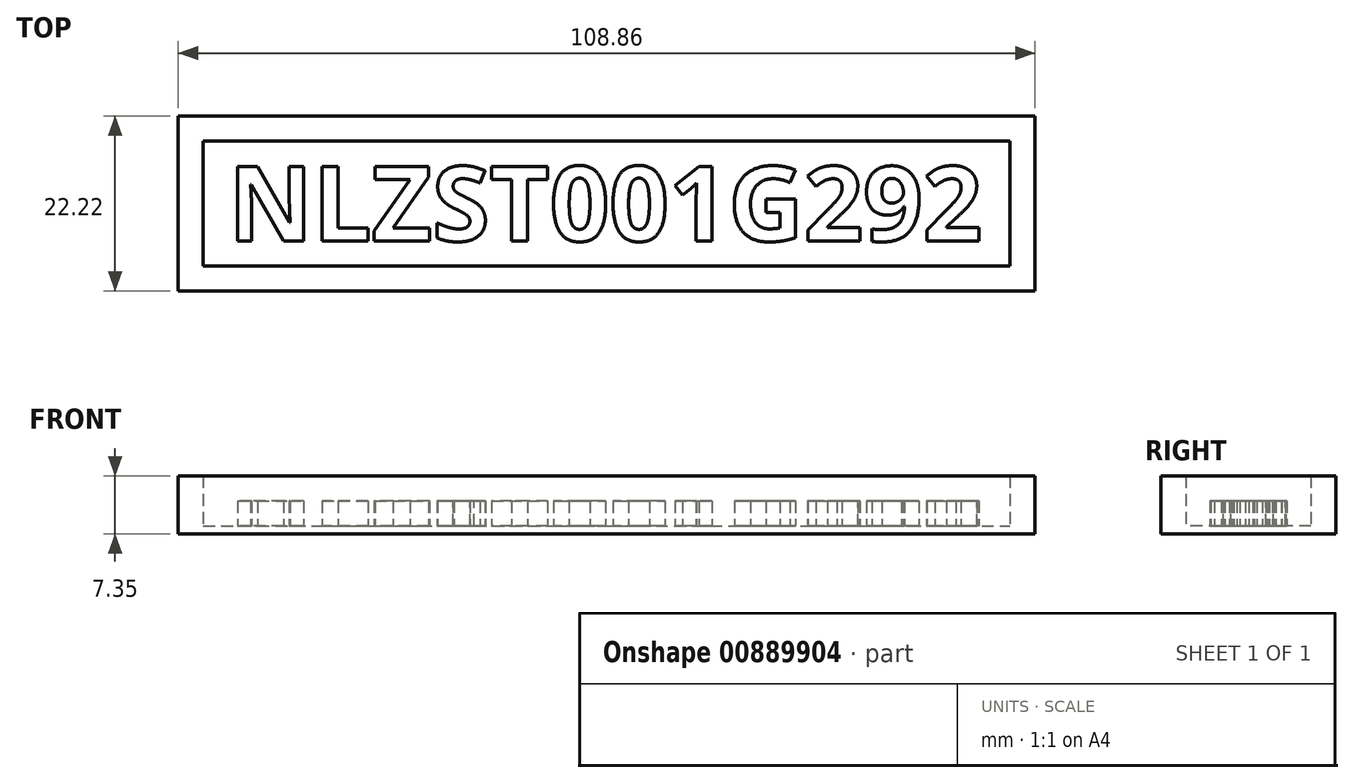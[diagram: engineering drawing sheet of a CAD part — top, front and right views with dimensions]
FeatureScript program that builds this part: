
annotation { "Feature Type Name" : "Feature", "Feature Type Description" : "" }
export const myFeature = defineFeature(function(context is Context, id is Id, definition is map)
    precondition{}
    {
        {
            var Q0;
            Q0=qCreatedBy(makeId("Top.planeOp"),FACE);
            var sketch = newSketch(context, id + "F0", { "sketchPlane" : qUnion([Q0])});
            skText(sketch, "E0", { "text": "NLZST001G292", "fontName": "OpenSans-Bold.ttf"});
            skLineSegment(sketch, "E1.bottom", {"start": v(-52.36, -1.8) * mm, "end": v(50.15, -1.8) * mm, "construction": true});
            skLineSegment(sketch, "E1.top", {"start": v(-52.36, 14.08) * mm, "end": v(50.15, 14.08) * mm, "construction": true});
            skLineSegment(sketch, "E1.left", {"start": v(-52.36, -1.8) * mm, "end": v(-52.36, 14.08) * mm, "construction": true});
            skLineSegment(sketch, "E1.right", {"start": v(50.15, -1.8) * mm, "end": v(50.15, 14.08) * mm, "construction": true});
            const initialGuessF0  = {"E0": [-0.04919, 0.00138, 1, 0, 0.00953]};
            skSetInitialGuess(sketch, initialGuessF0);
            skSolve(sketch);
        }
        {
            var Q0;
            Q0=qCreatedBy(makeId("Top.planeOp"),FACE);
            var sketch = newSketch(context, id + "F1", { "sketchPlane" : qUnion([Q0])});
            skLineSegment(sketch, "E2.bottom", {"start": v(-52.36, 14.08) * mm, "end": v(50.15, 14.08) * mm});
            skLineSegment(sketch, "E2.top", {"start": v(-52.36, -1.8) * mm, "end": v(50.15, -1.8) * mm});
            skLineSegment(sketch, "E2.left", {"start": v(-52.36, 14.08) * mm, "end": v(-52.36, -1.8) * mm});
            skLineSegment(sketch, "E2.right", {"start": v(50.15, 14.08) * mm, "end": v(50.15, -1.8) * mm});
            skSolve(sketch);
        }
        {
            var Q0;
            Q0 = qSketchRegion(id + "F1", true);
            extrude(context, id + "F2", {"entities" : qUnion([Q0]), "oppositeDirection" : true, "depth" : 1 * mm, "offsetDistance" : 25.4 * mm});
        }
        {
            var Q0;
            Q0 = qSketchRegion(id + "F0", true);
            extrude(context, id + "F3", {"entities" : qUnion([Q0]), "operationType" : NewBodyOperationType.ADD, "depth" : 3.17 * mm, "offsetDistance" : 25.4 * mm});
        }
        {
            var Q0;
            Q0=qCreatedBy(makeId("Top.planeOp"),FACE);
            var sketch = newSketch(context, id + "F4", { "sketchPlane" : qUnion([Q0])});
            skLineSegment(sketch, "E3.bottom", {"start": v(50.15, 14.08) * mm, "end": v(-52.36, 14.08) * mm});
            skLineSegment(sketch, "E3.top", {"start": v(50.15, -1.8) * mm, "end": v(-52.36, -1.8) * mm});
            skLineSegment(sketch, "E3.left", {"start": v(50.15, -1.8) * mm, "end": v(50.15, 14.08) * mm});
            skLineSegment(sketch, "E3.right", {"start": v(-52.36, -1.8) * mm, "end": v(-52.36, 14.08) * mm});
            skLineSegment(sketch, "E4", {"start": v(50.15, 6.14) * mm, "end": v(-1.1, 6.14) * mm, "construction": true});
            skLineSegment(sketch, "E5", {"start": v(-1.1, 6.14) * mm, "end": v(-1.1, 14.08) * mm, "construction": true});
            skLineSegment(sketch, "E6.bottom", {"start": v(-55.54, -4.97) * mm, "end": v(53.32, -4.97) * mm});
            skLineSegment(sketch, "E6.top", {"start": v(-55.54, 17.25) * mm, "end": v(53.32, 17.25) * mm});
            skLineSegment(sketch, "E6.left", {"start": v(-55.54, 17.25) * mm, "end": v(-55.54, -4.97) * mm});
            skLineSegment(sketch, "E6.right", {"start": v(53.32, 17.25) * mm, "end": v(53.32, -4.97) * mm});
            skPoint(sketch, "E6.middle", {"position": v(-1.1, 6.14) * mm});
            skSolve(sketch);
        }
        {
            var Q0;
            Q0 = qSketchRegion(id + "F4", true);
            var Q1;
            Q1=makeQuery(id+"F2.opExtrude","CAP_FACE",FACE,{"disambiguationData":[OSD([sQuery(id+"F1.wireOp",EDGE,"E2.bottom"),sQuery(id+"F1.wireOp",EDGE,"E2.top"),sQuery(id+"F1.wireOp",EDGE,"E2.left"),sQuery(id+"F1.wireOp",EDGE,"E2.right")])],"isStart":false});
            extrude(context, id + "F5", {"entities" : qUnion([Q0]), "operationType" : NewBodyOperationType.ADD, "depth" : 6.35 * mm, "offsetDistance" : 25.4 * mm, "hasSecondDirection" : true, "secondDirectionBound" : SecondDirectionBoundingType.UP_TO_SURFACE, "secondDirectionOppositeDirection" : true, "secondDirectionDepth" : 25.4 * mm, "secondDirectionBoundEntityFace" : qUnion([Q1])});
        }
    });
